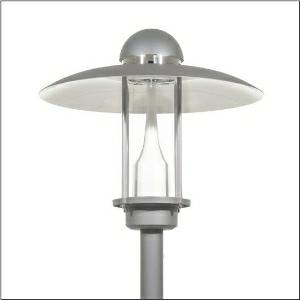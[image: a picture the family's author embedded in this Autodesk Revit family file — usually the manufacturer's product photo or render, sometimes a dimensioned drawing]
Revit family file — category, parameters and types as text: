
# Revit family: city-light_elegance_iq___p1_0a_5xa5265ff14h_a346
name_source: partatom
category: Lighting Fixtures
units: mm (PartAtom-declared; Revit-internal decimal feet)

## family parameters
Cut with Voids When Loaded = No
Host = Face
Light Source = No
Part Type = Normal
Room Calculation Point = No
Round Connector Dimension = Use Diameter
Shared = No

## types (1)
- --- (1 x LED, 1440 lm, 10.5 W, 3000K)
    Apparent Load = 11 VA
    CIE Flux Codes = 32 62 91 97 100
    Color Rendering = 70
    Color Temperature = 3000K
    Default Elevation = 1800 mm
    Description = City-Light Elegance iQ, mast luminaire, Module 540 iQ-SR, primary light control with 3 zone facetted reflector, of plastic, silver coated, highly specular, structured, primary optical cover: cover, of PMMA, transparent, light distribution: P1.0a, light emission: direct distribution, primary light characteristic: strongly asymmetric, installation type: post-top, LED, High Power LED, rated luminous flux: 1.440lm, luminous efficacy: 137lm/W, light colour: 730, colour temperature: 3000K, control gear: iQ Street-Remote, control: Auto-Match, Temp-Guard, Lumen-Switch, Night-Set, Smart-Wire, Light-Fading, Desk-Remote (wireless, voltage-free reading and setting of iQ features in the workshop via application-optimized NFC function/RFID function), optimised constant luminous flux control (CLO 2.0), Street-Remote, pre-setting: logarithmic dimming characteristic, with terminal, 6-pole, max. 2.5mm², mains connection: 230..240V, AC, 50/60Hz, start of lifetime: 11W, end of service life: 11W, reduction: 5W, luminaire housing, upper part, of aluminium, coated, Siteco® metallic grey (DB 702S), diameter: 750mm, height: 675mm, spigot size: d x l = 76 x 70mm (post-top) | with reducer (optional accessory) 60 x 70mm, mounting height: 3..5m, post-top mast mounting element, of diecast aluminium, coated, Siteco® metallic grey (DB 702S), Module 540 iQ-SR, traffic white (RAL 9016), equipment: standard, protection rating (complete): IP65, insulation class (complete): insulation class II (safety insulation), certification: CE, ENEC, VDE, packaging unit: 1 piece

Light Distribution: P1.0a
    Height = 675 mm
    Lamp = 1 x LED
    Lamp Light Flux = 1440 lm
    Lamp Power = 10.5 W
    Lamp count = 1
    Length = 750 mm
    Luminous efficacy = 137 lm/W
    Manufacturer = Siteco
    ModVariant = No
    Model = 5XA5265FF14H
    Number of Poles = 1
    OnlyDefault = Yes
    Power Factor = 1
    Product Name = City-Light Elegance iQ | P1.0a
    Product group = mast luminaire | pylon top
    ProductGroupID = 6100
    Protection Class = Protection class II
    Protection Degree = IP 65
    RLX_Detail_Level = 1
    RLX_Emergency_Light_Flux = 0 lm
    RLX_Emergency_Type = 0
    RLX_Emergency_Type_DB = No
    RlxData = <blob elided: 101873 chars, md5=8ffa696a>
    Socket = socket
    Standby Power = 0 W
    System Light Flux = 1440 lm
    System Power = 11 W
    Type Comments = factory setting: luminous flux: 100 % | dim-lin: 254 | 419 mA
    Type Image = l_1006912.jpg
    URL = http://relux.com
    VarID = @adj_181191
    Voltage = 0 V
    Weight = 0.00 kg
    Width = 0 mm  [stored 0 ft]

note: [stored X ft] marks values corroborated as IEEE doubles in the binary element streams (Revit-internal decimal feet)

## geometry (parser evidence)
native form markers: Blend x4, Sweep x11
no freeform markers — native parametric forms only
